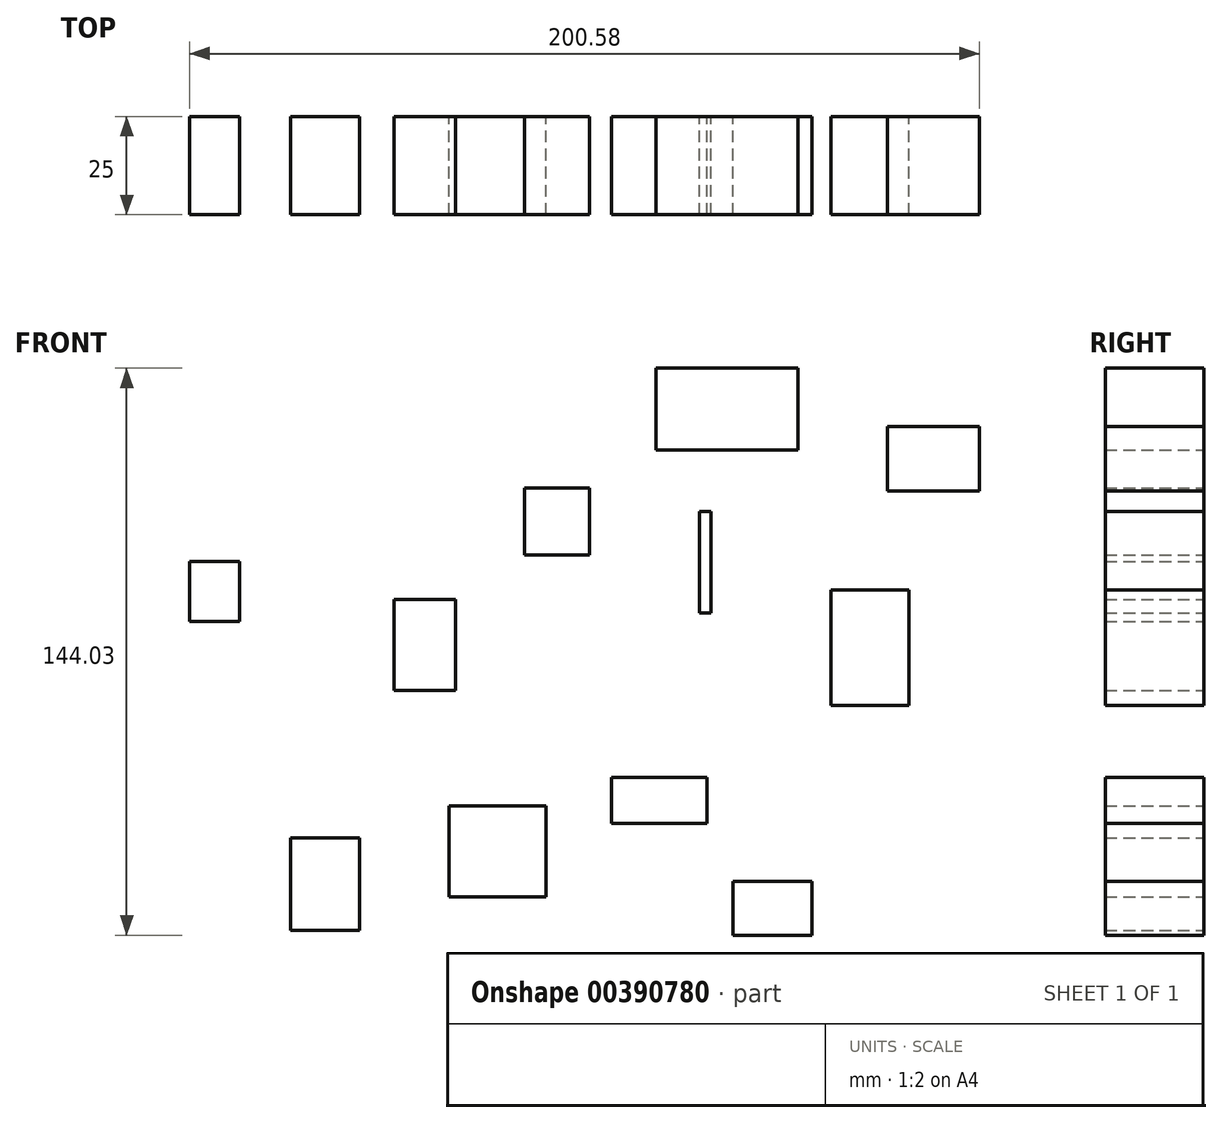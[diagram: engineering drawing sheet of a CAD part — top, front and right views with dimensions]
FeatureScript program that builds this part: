
annotation { "Feature Type Name" : "Feature", "Feature Type Description" : "" }
export const myFeature = defineFeature(function(context is Context, id is Id, definition is map)
    precondition{}
    {
        {
            var Q0;
            Q0=qCreatedBy(makeId("Front.planeOp"),FACE);
            var sketch = newSketch(context, id + "F0", { "sketchPlane" : qUnion([Q0])});
            skLineSegment(sketch, "E0.bottom", {"start": v(-123, 44.33) * mm, "end": v(-110.35, 44.33) * mm});
            skLineSegment(sketch, "E0.top", {"start": v(-123, 29.16) * mm, "end": v(-110.35, 29.16) * mm});
            skLineSegment(sketch, "E0.left", {"start": v(-123, 44.33) * mm, "end": v(-123, 29.16) * mm});
            skLineSegment(sketch, "E0.right", {"start": v(-110.35, 44.33) * mm, "end": v(-110.35, 29.16) * mm});
            skLineSegment(sketch, "E1.bottom", {"start": v(-97.37, -25.84) * mm, "end": v(-79.84, -25.84) * mm});
            skLineSegment(sketch, "E1.top", {"start": v(-97.37, -49.34) * mm, "end": v(-79.84, -49.34) * mm});
            skLineSegment(sketch, "E1.left", {"start": v(-97.37, -25.84) * mm, "end": v(-97.37, -49.34) * mm});
            skLineSegment(sketch, "E1.right", {"start": v(-79.84, -25.84) * mm, "end": v(-79.84, -49.34) * mm});
            skLineSegment(sketch, "E2.bottom", {"start": v(-71.08, 34.66) * mm, "end": v(-55.5, 34.66) * mm});
            skLineSegment(sketch, "E2.top", {"start": v(-71.08, 11.57) * mm, "end": v(-55.5, 11.57) * mm});
            skLineSegment(sketch, "E2.left", {"start": v(-71.08, 34.66) * mm, "end": v(-71.08, 11.57) * mm});
            skLineSegment(sketch, "E2.right", {"start": v(-55.5, 34.66) * mm, "end": v(-55.5, 11.57) * mm});
            skLineSegment(sketch, "E3.bottom", {"start": v(-37.97, 63.04) * mm, "end": v(-21.42, 63.04) * mm});
            skLineSegment(sketch, "E3.top", {"start": v(-37.97, 46.07) * mm, "end": v(-21.42, 46.07) * mm});
            skLineSegment(sketch, "E3.left", {"start": v(-37.97, 63.04) * mm, "end": v(-37.97, 46.07) * mm});
            skLineSegment(sketch, "E3.right", {"start": v(-21.42, 63.04) * mm, "end": v(-21.42, 46.07) * mm});
            skLineSegment(sketch, "E4.bottom", {"start": v(6.5, 57.05) * mm, "end": v(9.41, 57.05) * mm});
            skLineSegment(sketch, "E4.top", {"start": v(6.5, 31.28) * mm, "end": v(9.41, 31.28) * mm});
            skLineSegment(sketch, "E4.left", {"start": v(6.5, 57.05) * mm, "end": v(6.5, 31.28) * mm});
            skLineSegment(sketch, "E4.right", {"start": v(9.41, 57.05) * mm, "end": v(9.41, 31.28) * mm});
            skLineSegment(sketch, "E5.bottom", {"start": v(39.92, 37.16) * mm, "end": v(59.72, 37.16) * mm});
            skLineSegment(sketch, "E5.top", {"start": v(39.92, 7.83) * mm, "end": v(59.72, 7.83) * mm});
            skLineSegment(sketch, "E5.left", {"start": v(39.92, 37.16) * mm, "end": v(39.92, 7.83) * mm});
            skLineSegment(sketch, "E5.right", {"start": v(59.72, 37.16) * mm, "end": v(59.72, 7.83) * mm});
            skLineSegment(sketch, "E6.bottom", {"start": v(14.93, -36.9) * mm, "end": v(35.05, -36.9) * mm});
            skLineSegment(sketch, "E6.top", {"start": v(14.93, -50.57) * mm, "end": v(35.05, -50.57) * mm});
            skLineSegment(sketch, "E6.left", {"start": v(14.93, -36.9) * mm, "end": v(14.93, -50.57) * mm});
            skLineSegment(sketch, "E6.right", {"start": v(35.05, -36.9) * mm, "end": v(35.05, -50.57) * mm});
            skLineSegment(sketch, "E7.bottom", {"start": v(-57.12, -17.79) * mm, "end": v(-32.46, -17.79) * mm});
            skLineSegment(sketch, "E7.top", {"start": v(-57.12, -40.85) * mm, "end": v(-32.46, -40.85) * mm});
            skLineSegment(sketch, "E7.left", {"start": v(-57.12, -17.79) * mm, "end": v(-57.12, -40.85) * mm});
            skLineSegment(sketch, "E7.right", {"start": v(-32.46, -17.79) * mm, "end": v(-32.46, -40.85) * mm});
            skLineSegment(sketch, "E8.bottom", {"start": v(-15.9, -10.43) * mm, "end": v(8.44, -10.43) * mm});
            skLineSegment(sketch, "E8.top", {"start": v(-15.9, -22.23) * mm, "end": v(8.44, -22.23) * mm});
            skLineSegment(sketch, "E8.left", {"start": v(-15.9, -10.43) * mm, "end": v(-15.9, -22.23) * mm});
            skLineSegment(sketch, "E8.right", {"start": v(8.44, -10.43) * mm, "end": v(8.44, -22.23) * mm});
            skLineSegment(sketch, "E9.bottom", {"start": v(54.2, 78.61) * mm, "end": v(77.57, 78.61) * mm});
            skLineSegment(sketch, "E9.top", {"start": v(54.2, 62.31) * mm, "end": v(77.57, 62.31) * mm});
            skLineSegment(sketch, "E9.left", {"start": v(54.2, 78.61) * mm, "end": v(54.2, 62.31) * mm});
            skLineSegment(sketch, "E9.right", {"start": v(77.57, 78.61) * mm, "end": v(77.57, 62.31) * mm});
            skLineSegment(sketch, "E10.bottom", {"start": v(-4.54, 93.46) * mm, "end": v(31.48, 93.46) * mm});
            skLineSegment(sketch, "E10.top", {"start": v(-4.54, 72.7) * mm, "end": v(31.48, 72.7) * mm});
            skLineSegment(sketch, "E10.left", {"start": v(-4.54, 93.46) * mm, "end": v(-4.54, 72.7) * mm});
            skLineSegment(sketch, "E10.right", {"start": v(31.48, 93.46) * mm, "end": v(31.48, 72.7) * mm});
            skSolve(sketch);
        }
        {
            var Q0;
            Q0 = qSketchRegion(id + "F0", true);
            extrude(context, id + "F1", {"entities" : qUnion([Q0]), "depth" : 25 * mm});
        }
    });
